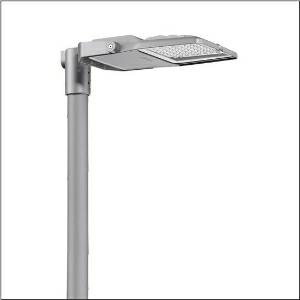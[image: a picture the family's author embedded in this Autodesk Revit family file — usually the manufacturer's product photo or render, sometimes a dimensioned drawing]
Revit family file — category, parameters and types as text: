
# Revit family: floodlight_fl_21_mini___pl43_5xa7776d2a3a_6ee6
name_source: partatom
category: Lighting Fixtures
units: mm (PartAtom-declared; Revit-internal decimal feet)

## family parameters
Cut with Voids When Loaded = No
Host = Face
Light Source = No
Part Type = Normal
Room Calculation Point = No
Round Connector Dimension = Use Diameter
Shared = No

## types (1)
- --- (1 x LED, 18300 lm, 142.9 W, 3000K)
    Apparent Load = 143 VA
    CIE Flux Codes = 27 78 99 100 100
    Color Rendering = 70
    Color Temperature = 3000K
    Default Elevation = 1800 mm
    Description = Floodlight FL 21 mini, floodlight, primary light control with lens, of PMMA, primary optical cover: protective disc, of toughened safety glass, transparent, light distribution: PL43, light emission: direct distribution, installation type: surface-mounted, LED, High Power LED, rated luminous flux: 18.300lm, luminous efficacy: 128lm/W, light colour: 730, colour temperature: 3000K, control gear: Smart Interface (Zhaga), control: flexible luminous flux parameterisation, time-dependent luminous flux control, constant luminous flux control, overheat protection, pre-setting: logarithmic dimming characteristic, with terminal, 6-pole, mains connection: 220..240V, AC, 50/60Hz, start of lifetime: 143W, end of service life: 151W, reduction: 63W, luminaire housing, of diecast aluminium, powder-coated, Siteco® metallic grey (DB 702S), corrosivity category C5 mid according to DIN EN ISO 12944, suitable for swimming pools, chlorine-resistant, sealing non-destructively replaceable, please order mast flange separately, mast bracket, of steel, galvanised, powder-coated, Siteco® metallic grey (DB 702S), Smart Interface below and above, protection rating (complete): IP66, insulation class (complete): insulation class II (safety insulation), certification: CE, ENEC, VDE, protection symbol: D, impact resistance: IK08, permissible operating ambient temperature: -40..+40°C, permissible operating ambient temperature for outdoor applications: -40..+50°C, standard: DIN EN 12944, LABS conformity tested according to VDMA 24364:2018-05, packaging unit: 1 piece

Light Distribution: PL43
    Height = 70 mm
    Lamp = 1 x LED
    Lamp Light Flux = 18300 lm
    Lamp Power = 142.9 W
    Lamp count = 1
    Length = 485 mm
    Luminous efficacy = 128 lm/W
    Manufacturer = Siteco
    ModVariant = No
    Model = 5XA7776D2A3A
    Number of Poles = 1
    OnlyDefault = Yes
    Power Factor = 1
    Product Name = Floodlight FL 21 mini | PL43
    Product group = floodlight | pylon annexe
    ProductGroupID = 6200
    Protection Class = Protection class II
    Protection Degree = IP 66
    RLX_Detail_Level = 1
    RLX_Emergency_Light_Flux = 0 lm
    RLX_Emergency_Type = 0
    RLX_Emergency_Type_DB = No
    RlxData = <blob elided: 101313 chars, md5=4b58bc2d>
    Socket = socket
    Standby Power = 0 W
    System Light Flux = 18300 lm
    System Power = 143 W
    Type Comments = factory setting: luminous flux: 100 % | dim-lin: 254 | 730 mA
    Type Image = l_1007125.jpg
    URL = http://relux.com
    VarID = @adj_160952
    Voltage = 0 V
    Weight = 0.00 kg
    Width = 337 mm

## geometry (parser evidence)
native form markers: Blend x4, Sweep x13
no freeform markers — native parametric forms only
